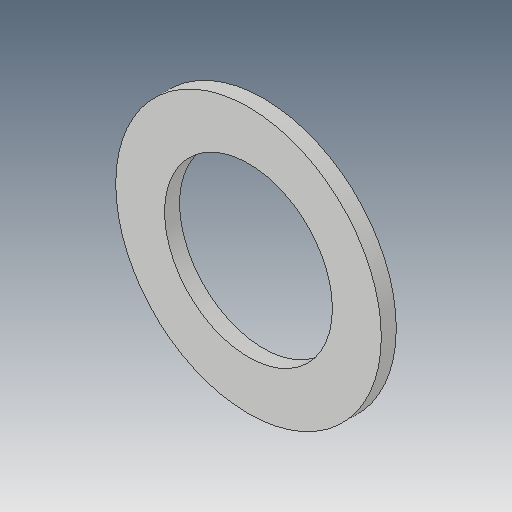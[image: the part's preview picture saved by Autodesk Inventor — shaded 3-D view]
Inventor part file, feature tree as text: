
AUTODESK INVENTOR PART (.ipt)
format: ipt  version: 2017 (Build 210142000, 142)  size: 90,624 bytes
history: native  units: mm
features: extrude x1, sketch x1
ambient origin geometry x8: Origin, YZ Plane, XZ Plane, XY Plane, X Axis, Y Axis, Z Axis, Center Point
bodies: Solid1 (feature_tree)
feature tree (2):
  extrude  "Extrusion1"  [1 undecoded]
  sketch  "Sketch1"  dims[d0=0.7mm d1=0.0mm]
note: 1 required parameter value undecoded (feature->parameter linkage not recoverable at this tier; creation-order binding heuristic only, values carry confidence <= 0.55)
